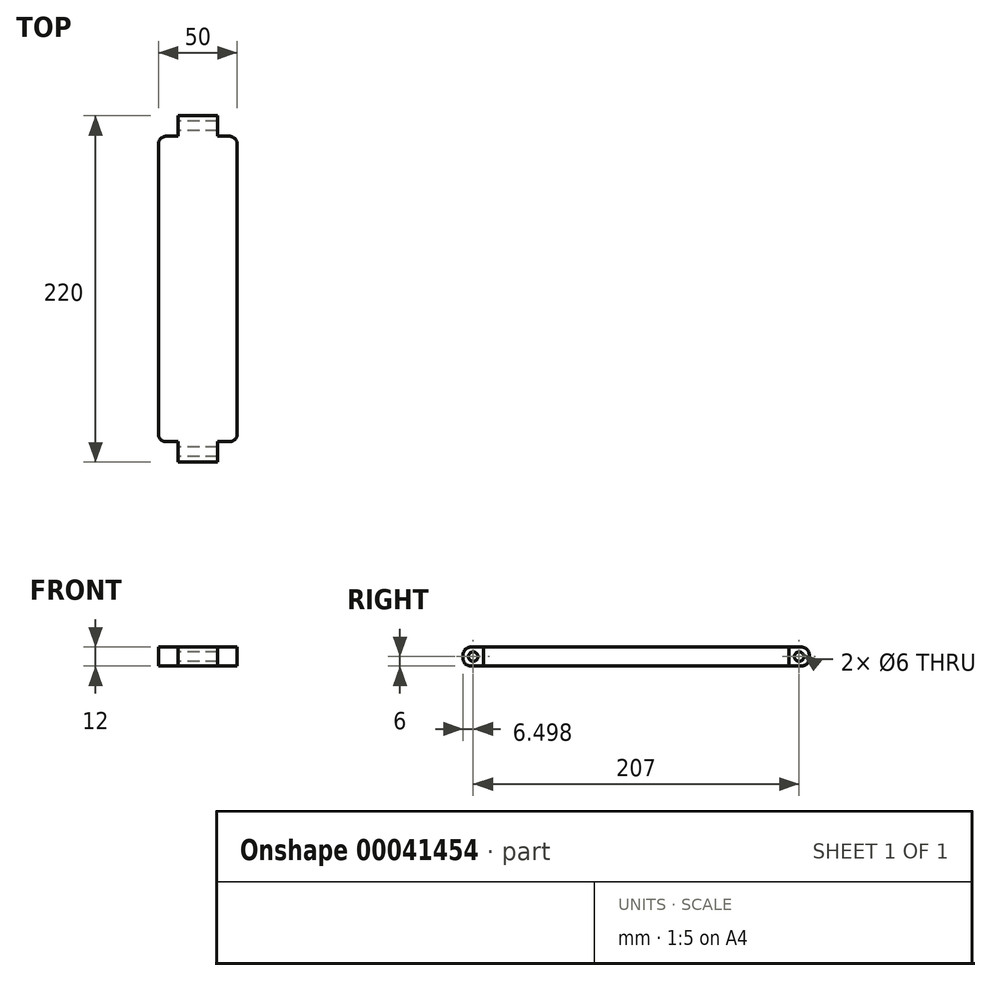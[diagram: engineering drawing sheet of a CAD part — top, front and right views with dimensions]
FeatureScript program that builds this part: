
annotation { "Feature Type Name" : "Feature", "Feature Type Description" : "" }
export const myFeature = defineFeature(function(context is Context, id is Id, definition is map)
    precondition{}
    {
        {
            var Q0;
            Q0=qCreatedBy(makeId("Top.planeOp"),FACE);
            var sketch = newSketch(context, id + "F0", { "sketchPlane" : qUnion([Q0])});
            skLineSegment(sketch, "E0.bottom", {"start": v(-41.08, 165.7) * mm, "end": v(-16.08, 165.7) * mm});
            skLineSegment(sketch, "E0.top", {"start": v(-41.08, -54.3) * mm, "end": v(-16.08, -54.3) * mm});
            skLineSegment(sketch, "E0.left", {"start": v(-53.58, 152.7) * mm, "end": v(-53.58, -41.3) * mm});
            skLineSegment(sketch, "E0.right", {"start": v(-3.58, 152.7) * mm, "end": v(-3.58, -41.3) * mm});
            skLineSegment(sketch, "E1.left", {"start": v(-41.08, -54.3) * mm, "end": v(-41.08, -41.3) * mm});
            skLineSegment(sketch, "E1.right", {"start": v(-16.08, -54.3) * mm, "end": v(-16.08, -41.3) * mm});
            skLineSegment(sketch, "E2.left", {"start": v(-41.08, 165.7) * mm, "end": v(-41.08, 152.7) * mm});
            skLineSegment(sketch, "E2.right", {"start": v(-16.08, 165.7) * mm, "end": v(-16.08, 152.7) * mm});
            skLineSegment(sketch, "E3", {"start": v(-41.08, 152.7) * mm, "end": v(-53.58, 152.7) * mm});
            skLineSegment(sketch, "E4", {"start": v(-16.08, 152.7) * mm, "end": v(-3.58, 152.7) * mm});
            skLineSegment(sketch, "E5", {"start": v(-53.58, -41.3) * mm, "end": v(-41.08, -41.3) * mm});
            skLineSegment(sketch, "E6.trimOffspring", {"start": v(-16.08, -41.3) * mm, "end": v(-3.58, -41.3) * mm});
            skSolve(sketch);
        }
        {
            var Q0;
            Q0=makeQuery(id+"F0.imprint","IMPRINT",FACE,{"disambiguationData":[TD([[makeQuery(id+"F0.imprint","IMPRINT",EDGE,{"derivedFrom":sQuery(id+"F0.wireOp",EDGE,"E0.left")}),1.0]])]});
            extrude(context, id + "F1", {"entities" : qUnion([Q0]), "depth" : 12 * mm});
        }
        {
            var Q0;
            Q0=makeQuery(id+"F1.opExtrude","SWEPT_FACE",FACE,{"disambiguationData":[OSD([sQuery(id+"F0.wireOp",EDGE,"E2.left")])]});
            var sketch = newSketch(context, id + "F2", { "sketchPlane" : qUnion([Q0])});
            skLineSegment(sketch, "E7", {"start": v(-165.7, 6) * mm, "end": v(-152.7, 6) * mm, "construction": true});
            skPoint(sketch, "E7.endSnap0", {"position": v(-152.7, 6) * mm});
            skLineSegment(sketch, "E8", {"start": v(-159.2, 12) * mm, "end": v(-159.2, 0) * mm, "construction": true});
            skPoint(sketch, "E8.startSnap0", {"position": v(-159.2, 12) * mm});
            skPoint(sketch, "E9.orphan", {"position": v(-201.55, 6) * mm});
            skPoint(sketch, "E10.orphan", {"position": v(-159.2, 12.48) * mm});
            skCircle(sketch, "E11", {"center": v(-159.2, 6) * mm, "radius": 3 * mm});
            skSolve(sketch);
        }
        {
            var Q0;
            Q0 = qSketchRegion(id + "F2", true);
            extrude(context, id + "F3", {"entities" : qUnion([Q0]), "operationType" : NewBodyOperationType.REMOVE, "endBound" : BoundingType.THROUGH_ALL, "oppositeDirection" : true, "depth" : 25 * mm});
        }
        {
            var Q0;
            Q0=makeQuery(id+"F1.opExtrude","SWEPT_FACE",FACE,{"disambiguationData":[OSD([sQuery(id+"F0.wireOp",EDGE,"E1.left")])]});
            var sketch = newSketch(context, id + "F4", { "sketchPlane" : qUnion([Q0])});
            skLineSegment(sketch, "E12", {"start": v(47.8, 0) * mm, "end": v(47.8, 12) * mm, "construction": true});
            skLineSegment(sketch, "E13", {"start": v(54.3, 6) * mm, "end": v(41.3, 6) * mm, "construction": true});
            skCircle(sketch, "E14", {"center": v(47.8, 6) * mm, "radius": 3 * mm});
            skSolve(sketch);
        }
        {
            var Q0;
            Q0 = qSketchRegion(id + "F4", true);
            extrude(context, id + "F5", {"entities" : qUnion([Q0]), "operationType" : NewBodyOperationType.REMOVE, "endBound" : BoundingType.THROUGH_ALL, "oppositeDirection" : true, "depth" : 25 * mm});
        }
        {
            var Q0;
            Q0=makeQuery(id+"F1.opExtrude","CAP_EDGE",EDGE,{"disambiguationData":[OSD([sQuery(id+"F0.wireOp",EDGE,"E0.top")])],"isStart":false});
            var Q1;
            Q1=makeQuery(id+"F1.opExtrude","CAP_EDGE",EDGE,{"disambiguationData":[OSD([sQuery(id+"F0.wireOp",EDGE,"E0.top")])],"isStart":true});
            var Q2;
            Q2=makeQuery(id+"F1.opExtrude","CAP_EDGE",EDGE,{"disambiguationData":[OSD([sQuery(id+"F0.wireOp",EDGE,"E0.bottom")])],"isStart":false});
            var Q3;
            Q3=makeQuery(id+"F1.opExtrude","CAP_EDGE",EDGE,{"disambiguationData":[OSD([sQuery(id+"F0.wireOp",EDGE,"E0.bottom")])],"isStart":true});
            var Q4;
            Q4=makeQuery(id+"F1.opExtrude","SWEPT_EDGE",EDGE,{"disambiguationData":[OSD([sQuery(id+"F0.wireOp",EDGE,"E0.right"),sQuery(id+"F0.wireOp",EDGE,"E4")])]});
            var Q5;
            Q5=makeQuery(id+"F1.opExtrude","SWEPT_EDGE",EDGE,{"disambiguationData":[OSD([sQuery(id+"F0.wireOp",EDGE,"E0.left"),sQuery(id+"F0.wireOp",EDGE,"E3")])]});
            var Q6;
            Q6=makeQuery(id+"F1.opExtrude","SWEPT_EDGE",EDGE,{"disambiguationData":[OSD([sQuery(id+"F0.wireOp",EDGE,"E0.left"),sQuery(id+"F0.wireOp",EDGE,"E5")])]});
            var Q7;
            Q7=makeQuery(id+"F1.opExtrude","SWEPT_EDGE",EDGE,{"disambiguationData":[OSD([sQuery(id+"F0.wireOp",EDGE,"E0.right"),sQuery(id+"F0.wireOp",EDGE,"E6.trimOffspring")])]});
            fillet(context, id + "F6", {"entities" : qUnion([Q0, Q1, Q2, Q3, Q4, Q5, Q6, Q7]), "radius" : 5 * mm, "tangentPropagation" : true, "allowEdgeOverflow" : false});
        }
    });
